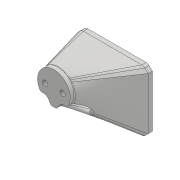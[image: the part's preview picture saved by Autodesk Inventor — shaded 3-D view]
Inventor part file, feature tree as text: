
AUTODESK INVENTOR PART (.ipt)
format: ipt  version: 2018 (Build 220112000, 112)  size: 1,684,480 bytes
history: native  units: mm
features: sketch x48, extrude x40, projected_geometry x39, fillet x13, hole x12, chamfer x10, plane x2, mirror x1, loft x1, other x1
ambient origin geometry x8: Origin, YZ Plane, XZ Plane, XY Plane, X Axis, Y Axis, Z Axis, Center Point
bodies: Solid1 (feature_tree), Solid2 (feature_tree)
feature tree (167):
  extrude  "Extrusion1"  Depth=45.0mm
  extrude  "Extrusion2"  Depth=2.25mm
  hole  "Hole1"  [1 undecoded]
  hole  "Hole2"  [1 undecoded]
  fillet  "Fillet1"  Radius=14.0mm
  extrude  "Extrusion3"  Depth=18.5mm
  extrude  "Extrusion4"  Depth=10.0mm
  extrude  "Extrusion5"  Depth=2.195mm
  extrude  "Extrusion6"  Depth=20.5mm
  hole  "Hole3"  [1 undecoded]
  extrude  "Extrusion7"  Depth=0.5mm
  extrude  "Extrusion8"  Depth=5.0mm TaperAngle=0.0deg
  extrude  "Extrusion9"  Depth=10.0mm
  extrude  "Extrusion10"  Depth=10.0mm
  extrude  "Extrusion11"  Depth=14.5mm
  extrude  "Extrusion12"  Depth=14.5mm
  extrude  "Extrusion13"  Depth=5.0mm
  extrude  "Extrusion14"  Depth=2.25mm
  extrude  "Extrusion15"  Depth=5.0mm
  extrude  "Extrusion16"  Depth=9.0mm
  extrude  "Extrusion17"  Depth=4.0mm
  chamfer  "Chamfer1"  Distance=1.0mm
  fillet  "Fillet7"  Radius=20.7mm
  fillet  "Fillet8"  Radius=32.0mm
  mirror  "Mirror1"
  extrude  "Extrusion19"  Depth=1.0mm TaperAngle=0.0deg
  extrude  "Extrusion20"  Depth=8.0mm
  extrude  "Extrusion21"  Depth=0.2mm TaperAngle=0.0deg
  extrude  "Extrusion22"  Depth=0.5mm TaperAngle=0.0deg
  sketch  "Sketch29"  dims[d77=12.25mm d78=0.0mm d80=8.0mm]
  extrude  "Extrusion23"  Depth=5.0mm TaperAngle=0.0deg
  extrude  "Extrusion24"  Depth=0.2mm TaperAngle=0.0deg
  plane  "Work Plane1"
  extrude  "Extrusion25"  Depth=2.5mm TaperAngle=45.0deg
  extrude  "Extrusion26"  Depth=0.5mm
  extrude  "Extrusion27"  Depth=8.0mm
  extrude  "Extrusion28"  Depth=3.0mm TaperAngle=0.0deg
  extrude  "Extrusion29"  Depth=33.0mm
  extrude  "Extrusion30"  Depth=56.0mm
  extrude  "Extrusion31"  Depth=25.0mm TaperAngle=0.0deg
  chamfer  "Chamfer2"  Distance=6.0mm
  hole  "Hole6"  [1 undecoded]
  chamfer  "Chamfer3"  Distance=40.0mm
  extrude  "Extrusion32"  Depth=12.0mm
  extrude  "Extrusion33"  Depth=40.0mm TaperAngle=0.0deg
  chamfer  "Chamfer4"  Distance=40.0mm
  chamfer  "Chamfer5"  Distance=1.8mm
  chamfer  "Chamfer6"  Distance=3.3mm
  fillet  "Fillet9"  Radius=14.0mm
  extrude  "Extrusion34"  Depth=1.2mm TaperAngle=45.0deg
  chamfer  "Chamfer7"  Distance=2.5mm
  sketch  "Sketch42"  dims[d146=6.0mm d147=0.0mm d149=42.0mm]
  hole  "Hole7"  [1 undecoded]
  hole  "Hole8"  [1 undecoded]
  hole  "Hole9"  [1 undecoded]
  fillet  "Fillet10"  Radius=3.0mm
  chamfer  "Chamfer8"  Distance=2.0mm
  chamfer  "Chamfer9"  Distance=12.0mm
  fillet  "Fillet11"  Radius=2.0mm
  fillet  "Fillet12"  Radius=15.0mm
  extrude  "Extrusion35"  Depth=10.0mm TaperAngle=0.0deg
  sketch  "Sketch45"  dims[d151=4.5mm]
  hole  "Hole10"  [1 undecoded]
  hole  "Hole11"  [1 undecoded]
  hole  "Hole12"  [1 undecoded]
  fillet  "Fillet13"  Radius=3.18mm
  fillet  "Fillet14"  Radius=3.18mm
  fillet  "Fillet15"  Radius=0.5mm
  chamfer  "Chamfer10"  Distance=2.0mm Angle=45.0deg
  extrude  "Extrusion36"  Depth=10.0mm TaperAngle=45.0deg
  sketch  "Sketch47"  dims[d155=28.0mm d156=12.0mm]
  extrude  "Extrusion37"  Depth=10.0mm
  extrude  "Extrusion38"  Depth=10.0mm
  plane  "Work Plane2"
  loft  "Loft1"
  hole  "Hole13"  [1 undecoded]
  extrude  "Extrusion39"  Depth=10.0mm TaperAngle=0.0deg
  extrude  "Extrusion40"  Depth=10.0mm
  fillet  "Fillet16"  Radius=2.75mm
  fillet  "Fillet17"  Radius=2.5mm
  extrude  "Extrusion41"  Depth=10.0mm
  fillet  "Fillet18"  Radius=2.0mm
  hole  "Hole14"  [1 undecoded]
  sketch  "Sketch1"  dims[d0=24.5mm d1=45.0mm]
  sketch  "Sketch2"  dims[d2=1.95mm d3=0.0mm d4=2.25mm]
  projected_geometry  "Projected Loop1"
  sketch  "Sketch3"  dims[d5=20.0mm d6=2.25mm]
  projected_geometry  "Projected Loop2"
  sketch  "Sketch4"  dims[d7=5.25mm d8=5.25mm d9=14.0mm]
  projected_geometry  "Projected Loop3"
  sketch  "Sketch5"  dims[d10=5.25mm d11=18.5mm]
  projected_geometry  "Projected Loop4"
  sketch  "Sketch6"  dims[d12=10.0mm d13=0.0mm d14=20.5mm]
  projected_geometry  "Projected Loop5"
  sketch  "Sketch7"  dims[d15=2.0mm d16=2.195mm]
  projected_geometry  "Projected Loop6"
  sketch  "Sketch8"  dims[d17=2.0mm]
  projected_geometry  "Projected Loop7"
  sketch  "Sketch9"  dims[d18=2.4mm d19=6.0mm d20=4.4mm d21=2.0mm d22=90.0deg d23=8.0mm d24=20.594885mm d25=20.5mm]
  projected_geometry  "Projected Loop8"
  projected_geometry  "Projected Loop9"
  sketch  "Sketch10"  dims[d26=26.65mm d27=2.0mm]
  projected_geometry  "Projected Loop10"
  projected_geometry  "Projected Loop11"
  sketch  "Sketch11"  dims[d28=2.0mm]
  projected_geometry  "Projected Loop12"
  sketch  "Sketch12"  dims[d29=2.4mm d30=6.0mm d31=4.4mm d32=2.0mm d33=90.0deg d34=8.0mm d35=20.594885mm d36=0.5mm]
  sketch  "Sketch13"  dims[d37=18.0mm d38=5.0mm d39=0.0mm]
  sketch  "Sketch14"  dims[d41=10.0mm d42=0.0mm d43=24.5mm]
  projected_geometry  "Projected Loop13"
  sketch  "Sketch15"  dims[d44=1.15mm d45=0.0mm d46=10.0mm]
  sketch  "Sketch16"  dims[d47=21.0mm d48=14.5mm]
  projected_geometry  "Projected Loop14"
  sketch  "Sketch17"  dims[d49=20.0mm d50=14.5mm]
  projected_geometry  "Projected Loop15"
  sketch  "Sketch18"  dims[d51=24.5mm d52=5.0mm]
  projected_geometry  "Projected Loop16"
  sketch  "Sketch19"  dims[d53=5.0mm d54=2.25mm]
  projected_geometry  "Projected Loop17"
  sketch  "Sketch20"  dims[d55=2.25mm d56=5.0mm]
  projected_geometry  "Projected Loop18"
  sketch  "Sketch25"  dims[d57=5.0mm d58=9.0mm]
  projected_geometry  "Projected Loop22"
  sketch  "Sketch26"  dims[d59=14.75mm d60=4.0mm d61=1.0mm d62=0.0mm d63=20.7mm]
  sketch  "Sketch27"  dims[d64=2.4mm d65=6.0mm d66=4.4mm d67=2.0mm d68=90.0deg d69=8.0mm d70=20.594885mm d72=32.0mm]
  projected_geometry  "Projected Loop23"
  sketch  "Sketch28"  dims[d73=5.0mm d74=0.0mm d75=1.0mm d76=0.0mm]
  projected_geometry  "Projected Loop24"
  sketch  "Sketch31"  dims[d81=4.5mm d82=0.0mm d84=0.2mm d85=0.0mm]
  projected_geometry  "Projected Loop25"
  sketch  "Sketch32"  dims[d86=21.0mm d87=0.5mm d88=0.0mm]
  projected_geometry  "Projected Loop26"
  sketch  "Sketch33"  dims[d91=8.0mm d92=0.0mm d93=5.0mm d94=0.0mm]
  sketch  "Sketch34"  dims[d95=5.0mm d96=0.0mm d98=0.2mm d99=0.0mm]
  sketch  "Sketch35"  dims[d100=0.2mm d101=0.0mm d102=2.5mm d103=2.0mm d104=45.0deg]
  projected_geometry  "Projected Loop27"
  sketch  "Sketch36"  dims[d105=1.5mm d114=0.5mm]
  sketch  "Sketch37"  dims[d128=4.0mm d129=0.0mm d130=8.0mm]
  sketch  "Sketch38"  dims[d131=3.0mm d132=0.0mm d133=3.0mm d134=0.0mm]
  projected_geometry  "Projected Loop28"
  sketch  "Sketch39"  dims[d135=25.0mm d136=0.0mm d137=33.0mm]
  projected_geometry  "Projected Loop29"
  sketch  "Sketch40"  dims[d138=2.5mm d139=56.0mm]
  projected_geometry  "Projected Loop30"
  sketch  "Sketch41"  dims[d140=25.0mm d141=0.0mm d142=25.0mm d143=0.0mm d144=6.0mm d145=0.0mm]
  sketch  "Sketch44"  dims[d150=4.5mm]
  projected_geometry  "Projected Loop31"
  projected_geometry  "Projected Loop32"
  projected_geometry  "Projected Loop33"
  sketch  "Sketch46"  dims[d152=4.5mm d153=40.0mm d154=0.0mm]
  projected_geometry  "Projected Loop34"
  sketch  "Sketch48"  dims[d157=12.0mm d158=40.0mm d159=0.0mm d160=40.0mm d161=0.0mm]
  projected_geometry  "Projected Loop35"
  sketch  "Sketch49"  dims[d162=20.5mm d163=1.8mm d164=0.0mm]
  other  "Edges1"
  sketch  "Sketch50"  dims[d165=20.5mm d166=3.3mm d167=0.0mm]
  projected_geometry  "Projected Loop36"
  sketch  "Sketch51"  dims[d168=2.0mm d169=2.0mm d170=45.0deg d171=14.0mm]
  projected_geometry  "Projected Loop37"
  sketch  "Sketch52"  dims[d172=3.1mm d173=6.0mm d174=6.3mm d175=2.0mm d176=90.0deg d177=8.0mm d178=20.594885mm d179=1.2mm d180=2.0mm d181=45.0deg]
  projected_geometry  "Projected Loop38"
  sketch  "Sketch53"  dims[d182=7.0mm d183=2.5mm d184=0.0mm]
  projected_geometry  "Projected Loop39"
  sketch  "Sketch54"  dims[d185=7.0mm d186=2.5mm d187=0.0mm d188=3.0mm d189=15.0mm d190=45.0deg d191=3.0mm d192=15.0mm d193=45.0deg d194=3.0mm d195=15.0mm d196=45.0deg d197=2.0mm d198=12.0mm d199=2.0mm d200=15.0mm d201=20.0mm d202=0.0mm d203=2.0mm d204=15.0mm d205=45.0deg d206=2.9mm d207=2.9mm d208=3.18mm d209=3.18mm d210=4.0mm d211=6.0mm d212=6.3mm d213=2.0mm d214=90.0deg d215=8.0mm d216=20.594885mm d217=1.567mm d218=25.0mm d219=6.3mm d220=2.0mm d221=90.0deg d222=25.0mm d223=20.594885mm d224=2.15mm d225=20.0mm d226=4.4mm d227=2.0mm d228=90.0deg d229=10.0mm d230=0.0mm d231=0.5mm d232=2.0mm d233=15.0mm d234=45.0deg d235=2.0mm d236=15.0mm d237=45.0deg d238=1.0mm d239=3.0mm d240=3.9mm d241=3.9mm d242=3.5mm d243=0.0mm d244=2.75mm d245=2.75mm d246=2.5mm d247=1.567mm d248=4.0mm d249=4.4mm d250=2.0mm d251=90.0deg d252=40.0mm d253=20.594885mm d254=2.1mm d255=4.0mm d256=4.4mm d257=2.0mm d258=90.0deg d259=28.25mm d260=0.0mm d261=3.9mm d262=4.0mm d263=4.4mm d264=2.0mm d265=90.0deg d266=20.0mm d267=0.0mm d268=0.2mm d269=2.0mm d270=2.0mm d271=1.8mm d272=15.0mm d273=45.0deg d274=2.0mm d275=0.0mm d276=20.0mm d277=4.2mm d278=0.0mm d279=5.0mm d280=0.0mm d281=25.0mm d282=15.0mm d283=0.0mm d284=90.0deg d285=0.0mm d286=90.0deg d287=14.0mm d288=9.899495mm d289=9.899495mm d290=3.3mm d291=6.0mm d292=6.3mm d293=2.0mm d294=90.0deg d295=8.0mm d296=20.594885mm d297=7.0mm d298=3.0mm d299=0.0mm d300=6.5mm d301=6.5mm d302=6.5mm d303=6.5mm d304=23.0mm d305=0.0mm d306=1.0mm d307=1.0mm d308=2.0mm d309=0.0mm d310=2.0mm d311=8.0mm d312=2.459mm d313=15.0mm d314=6.3mm d315=2.0mm d316=90.0deg d317=15.0mm d318=20.594885mm]
  projected_geometry  "Project Cut Edges1"
  projected_geometry  "Project Cut Edges2"
  projected_geometry  "Project Cut Edges3"
note: 12 required parameter values undecoded (feature->parameter linkage not recoverable at this tier; creation-order binding heuristic only, values carry confidence <= 0.55)
